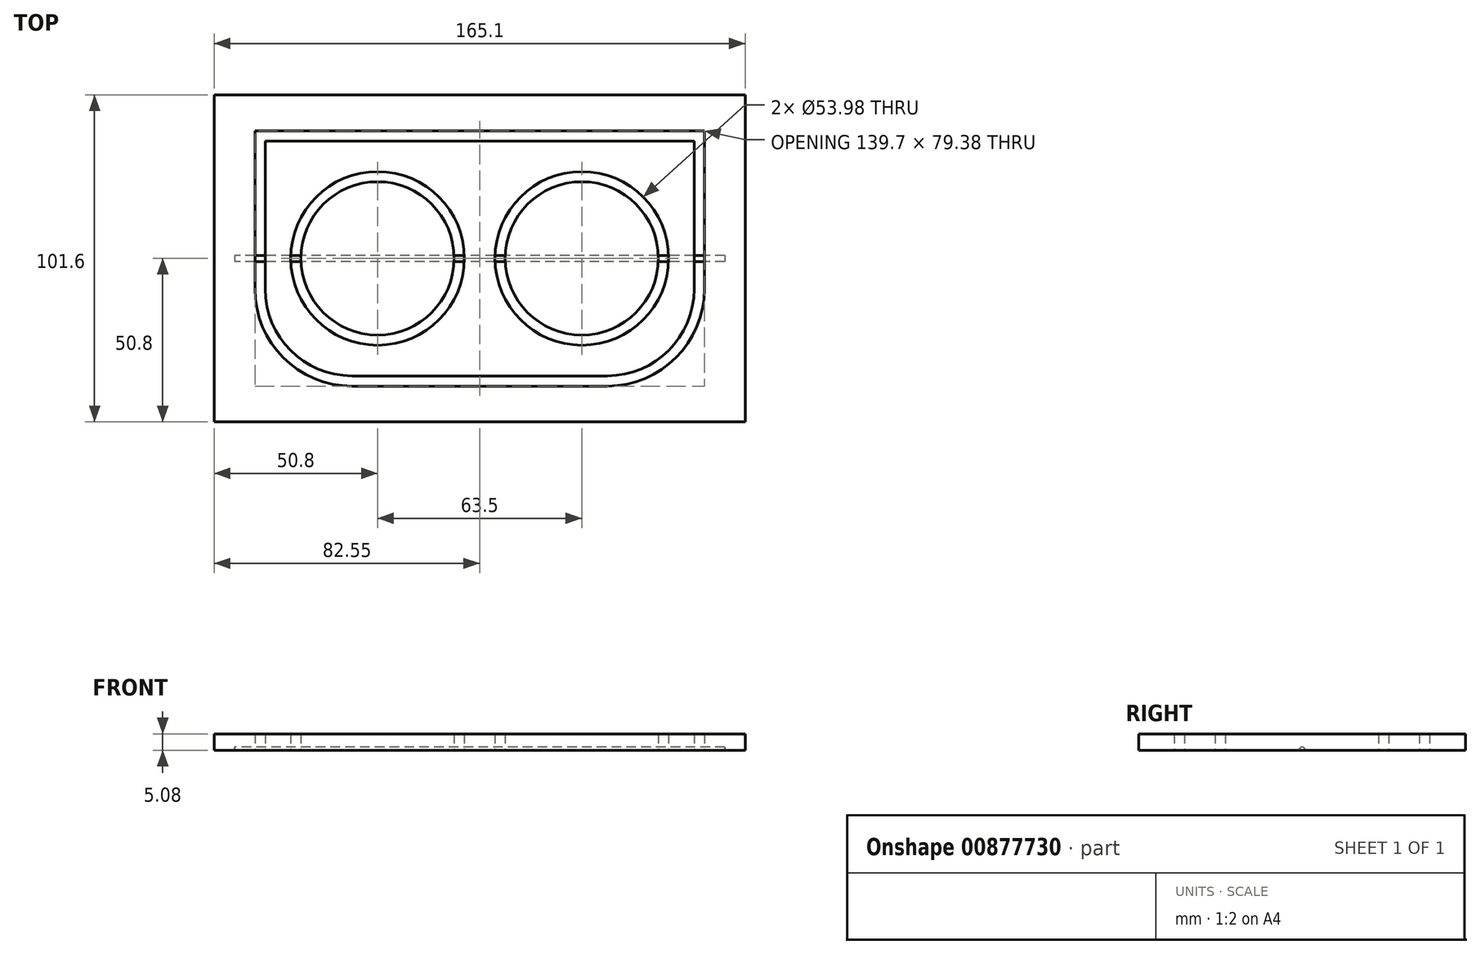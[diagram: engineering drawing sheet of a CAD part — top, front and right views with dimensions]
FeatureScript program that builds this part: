
annotation { "Feature Type Name" : "Feature", "Feature Type Description" : "" }
export const myFeature = defineFeature(function(context is Context, id is Id, definition is map)
    precondition{}
    {
        {
            var Q0;
            Q0=qCreatedBy(makeId("Top.planeOp"),FACE);
            var sketch = newSketch(context, id + "F0", { "sketchPlane" : qUnion([Q0])});
            skCircle(sketch, "E0", {"center": v(31.75, 0) * mm, "radius": 26.99 * mm});
            skCircle(sketch, "E1.1.0.0", {"center": v(-31.75, 0) * mm, "radius": 26.99 * mm});
            skLineSegment(sketch, "E1.direction1", {"start": v(31.75, 0) * mm, "end": v(-31.75, 0) * mm, "construction": true});
            skLineSegment(sketch, "E2.bottom", {"start": v(-66.67, 36.51) * mm, "end": v(66.68, 36.51) * mm});
            skLineSegment(sketch, "E2.top", {"start": v(-39.72, -36.51) * mm, "end": v(39.69, -36.51) * mm});
            skLineSegment(sketch, "E2.left", {"start": v(-66.67, 36.51) * mm, "end": v(-66.68, -9.56) * mm});
            skLineSegment(sketch, "E2.right", {"start": v(66.68, 36.51) * mm, "end": v(66.68, -9.53) * mm});
            skPoint(sketch, "E2.middle", {"position": v(0, 0) * mm});
            skPoint(sketch, "E3.visualSharp", {"position": v(-66.68, -36.51) * mm});
            skArc(sketch, "E3.filletArc", {"start": v(-66.68, -9.56) * mm, "mid": v(-58.78, -28.62) * mm, "end": v(-39.72, -36.51) * mm});
            skPoint(sketch, "E4.visualSharp", {"position": v(66.68, -36.51) * mm});
            skArc(sketch, "E4.filletArc", {"start": v(39.69, -36.51) * mm, "mid": v(58.77, -28.6) * mm, "end": v(66.68, -9.53) * mm});
            skCircle(sketch, "E5", {"center": v(31.75, 0) * mm, "radius": 23.81 * mm});
            skCircle(sketch, "E6", {"center": v(-31.75, 0) * mm, "radius": 23.81 * mm});
            skLineSegment(sketch, "E7.0", {"start": v(-73.02, 42.86) * mm, "end": v(-73.03, -9.56) * mm});
            skLineSegment(sketch, "E7.1", {"start": v(73.03, 42.86) * mm, "end": v(73.03, -9.53) * mm});
            skArc(sketch, "E7.2", {"start": v(39.69, -42.86) * mm, "mid": v(63.26, -33.1) * mm, "end": v(73.03, -9.53) * mm});
            skLineSegment(sketch, "E7.3", {"start": v(-73.02, 42.86) * mm, "end": v(73.03, 42.86) * mm});
            skLineSegment(sketch, "E7.4", {"start": v(-39.72, -42.86) * mm, "end": v(39.69, -42.86) * mm});
            skArc(sketch, "E7.5", {"start": v(-73.03, -9.56) * mm, "mid": v(-63.27, -33.1) * mm, "end": v(-39.72, -42.86) * mm});
            skLineSegment(sketch, "E8.bottom", {"start": v(-82.55, 50.8) * mm, "end": v(82.55, 50.8) * mm});
            skLineSegment(sketch, "E8.top", {"start": v(-82.55, -50.8) * mm, "end": v(82.55, -50.8) * mm});
            skLineSegment(sketch, "E8.left", {"start": v(-82.55, 50.8) * mm, "end": v(-82.55, -50.8) * mm});
            skLineSegment(sketch, "E8.right", {"start": v(82.55, 50.8) * mm, "end": v(82.55, -50.8) * mm});
            skPoint(sketch, "E9", {"position": v(-55.56, 0) * mm});
            skPoint(sketch, "E10", {"position": v(-58.74, 0) * mm});
            skLineSegment(sketch, "E11.0", {"start": v(-69.85, 39.69) * mm, "end": v(69.85, 39.69) * mm});
            skArc(sketch, "E11.1", {"start": v(-69.85, -9.56) * mm, "mid": v(-61.02, -30.86) * mm, "end": v(-39.72, -39.69) * mm});
            skLineSegment(sketch, "E11.2", {"start": v(-39.72, -39.69) * mm, "end": v(39.69, -39.69) * mm});
            skLineSegment(sketch, "E11.3", {"start": v(-69.85, 39.69) * mm, "end": v(-69.85, -9.56) * mm});
            skArc(sketch, "E11.4", {"start": v(39.69, -39.69) * mm, "mid": v(61.02, -30.85) * mm, "end": v(69.85, -9.53) * mm});
            skLineSegment(sketch, "E11.5", {"start": v(69.85, 39.69) * mm, "end": v(69.85, -9.53) * mm});
            skSolve(sketch);
        }
        {
            var Q0;
            Q0=makeQuery(id+"F0.imprint","IMPRINT",FACE,{"disambiguationData":[TD([[makeQuery(id+"F0.imprint","IMPRINT",EDGE,{"derivedFrom":sQuery(id+"F0.wireOp",EDGE,"E0")}),-1.0]])]});
            var Q1;
            Q1=makeQuery(id+"F0.imprint","IMPRINT",FACE,{"disambiguationData":[TD([[makeQuery(id+"F0.imprint","IMPRINT",EDGE,{"derivedFrom":sQuery(id+"F0.wireOp",EDGE,"E6")}),1.0]])]});
            var Q2;
            Q2=makeQuery(id+"F0.imprint","IMPRINT",FACE,{"disambiguationData":[TD([[makeQuery(id+"F0.imprint","IMPRINT",EDGE,{"derivedFrom":sQuery(id+"F0.wireOp",EDGE,"E5")}),1.0]])]});
            var Q3;
            Q3=makeQuery(id+"F0.imprint","IMPRINT",FACE,{"disambiguationData":[TD([[makeQuery(id+"F0.imprint","IMPRINT",EDGE,{"derivedFrom":sQuery(id+"F0.wireOp",EDGE,"E7.0")}),-1.0]])]});
            var Q4;
            Q4=makeQuery(id+"F0.imprint","IMPRINT",FACE,{"disambiguationData":[TD([[makeQuery(id+"F0.imprint","IMPRINT",EDGE,{"derivedFrom":sQuery(id+"F0.wireOp",EDGE,"E7.0")}),1.0]])]});
            extrude(context, id + "F1", {"entities" : qUnion([Q0, Q1, Q2, Q3, Q4]), "depth" : 5.08 * mm, "offsetDistance" : 25.4 * mm});
        }
        {
            var Q0;
            Q0=qCreatedBy(makeId("Right.planeOp"),FACE);
            var sketch = newSketch(context, id + "F2", { "sketchPlane" : qUnion([Q0])});
            skArc(sketch, "E12", {"start": v(0.95, 0) * mm, "mid": v(0, 0.95) * mm, "end": v(-0.95, 0) * mm});
            skPoint(sketch, "E13", {"position": v(-0.95, 0) * mm});
            skPoint(sketch, "E14", {"position": v(0.95, 0) * mm});
            skLineSegment(sketch, "E15", {"start": v(0.95, 0) * mm, "end": v(-0.95, 0) * mm});
            skSolve(sketch);
        }
        {
            var Q0;
            Q0=makeQuery(id+"F2.imprint","IMPRINT",FACE,{"disambiguationData":[TD([[makeQuery(id+"F2.imprint","IMPRINT",EDGE,{"derivedFrom":sQuery(id+"F2.wireOp",EDGE,"E12")}),1.0]])]});
            extrude(context, id + "F3", {"entities" : qUnion([Q0]), "depth" : 76.2 * mm, "offsetDistance" : 25.4 * mm, "hasSecondDirection" : true, "secondDirectionOppositeDirection" : true, "secondDirectionDepth" : 76.2 * mm});
        }
    });
